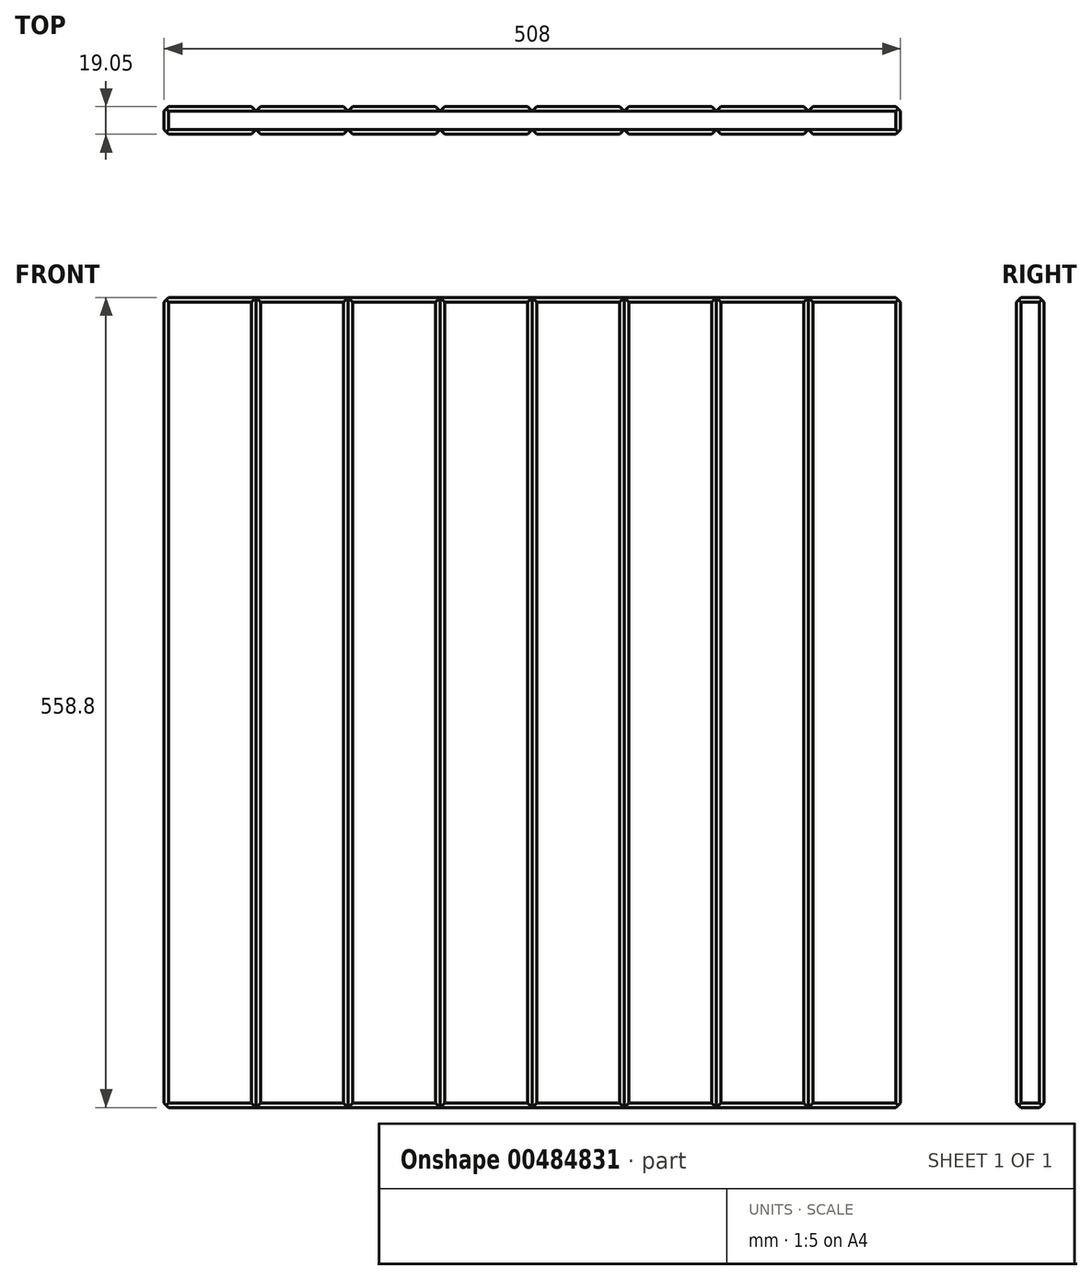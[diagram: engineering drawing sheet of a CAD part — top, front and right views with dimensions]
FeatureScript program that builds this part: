
annotation { "Feature Type Name" : "Feature", "Feature Type Description" : "" }
export const myFeature = defineFeature(function(context is Context, id is Id, definition is map)
    precondition{}
    {
        {
            var Q0;
            Q0=qCreatedBy(makeId("Front.planeOp"),FACE);
            var sketch = newSketch(context, id + "F0", { "sketchPlane" : qUnion([Q0])});
            skLineSegment(sketch, "E0.bottom", {"start": v(254, 279.4) * mm, "end": v(-254, 279.4) * mm});
            skLineSegment(sketch, "E0.top", {"start": v(254, -279.4) * mm, "end": v(-254, -279.4) * mm});
            skLineSegment(sketch, "E0.left", {"start": v(254, 279.4) * mm, "end": v(254, -279.4) * mm});
            skLineSegment(sketch, "E0.right", {"start": v(-254, 279.4) * mm, "end": v(-254, -279.4) * mm});
            skPoint(sketch, "E0.middle", {"position": v(0, 0) * mm});
            skSolve(sketch);
        }
        {
            var Q0;
            Q0 = qSketchRegion(id + "F0", true);
            extrude(context, id + "F1", {"entities" : qUnion([Q0]), "depth" : 19.05 * mm});
        }
        {
            var Q0;
            Q0=makeQuery(id+"F1.opExtrude","SWEPT_FACE",FACE,{"disambiguationData":[OSD([sQuery(id+"F0.wireOp",EDGE,"E0.top")])]});
            var sketch = newSketch(context, id + "F2", { "sketchPlane" : qUnion([Q0])});
            skLineSegment(sketch, "E1", {"start": v(-254, 19.05) * mm, "end": v(-190.5, 19.05) * mm});
            skLineSegment(sketch, "E2", {"start": v(-190.5, 19.05) * mm, "end": v(-127, 19.05) * mm});
            skLineSegment(sketch, "E3", {"start": v(-127, 19.05) * mm, "end": v(-63.5, 19.05) * mm});
            skLineSegment(sketch, "E4", {"start": v(-63.5, 19.05) * mm, "end": v(0, 19.05) * mm});
            skLineSegment(sketch, "E5", {"start": v(0, 19.05) * mm, "end": v(63.5, 19.05) * mm});
            skLineSegment(sketch, "E6", {"start": v(63.5, 19.05) * mm, "end": v(127, 19.05) * mm});
            skLineSegment(sketch, "E7", {"start": v(127, 19.05) * mm, "end": v(190.5, 19.05) * mm});
            skLineSegment(sketch, "E8", {"start": v(-254, 19.05) * mm, "end": v(-254, 15.88) * mm});
            skLineSegment(sketch, "E9", {"start": v(190.5, 19.05) * mm, "end": v(187.32, 19.05) * mm});
            skLineSegment(sketch, "E10", {"start": v(187.32, 19.05) * mm, "end": v(193.67, 19.05) * mm});
            skLineSegment(sketch, "E11", {"start": v(193.67, 19.05) * mm, "end": v(190.5, 15.88) * mm});
            skLineSegment(sketch, "E12", {"start": v(190.5, 15.88) * mm, "end": v(187.32, 19.05) * mm});
            skLineSegment(sketch, "E13.1.0.0", {"start": v(127, 15.88) * mm, "end": v(123.83, 19.05) * mm});
            skLineSegment(sketch, "E13.1.0.1", {"start": v(130.17, 19.05) * mm, "end": v(127, 15.88) * mm});
            skLineSegment(sketch, "E13.1.0.2", {"start": v(123.82, 19.05) * mm, "end": v(130.17, 19.05) * mm});
            skLineSegment(sketch, "E13.1.0.3", {"start": v(127, 19.05) * mm, "end": v(123.82, 19.05) * mm});
            skLineSegment(sketch, "E13.2.0.0", {"start": v(63.5, 15.87) * mm, "end": v(60.33, 19.05) * mm});
            skLineSegment(sketch, "E13.2.0.1", {"start": v(66.67, 19.05) * mm, "end": v(63.5, 15.88) * mm});
            skLineSegment(sketch, "E13.2.0.2", {"start": v(60.32, 19.05) * mm, "end": v(66.67, 19.05) * mm});
            skLineSegment(sketch, "E13.2.0.3", {"start": v(63.5, 19.05) * mm, "end": v(60.32, 19.05) * mm});
            skLineSegment(sketch, "E13.3.0.0", {"start": v(0, 15.87) * mm, "end": v(-3.17, 19.05) * mm});
            skLineSegment(sketch, "E13.3.0.1", {"start": v(3.17, 19.05) * mm, "end": v(0, 15.88) * mm});
            skLineSegment(sketch, "E13.3.0.2", {"start": v(-3.18, 19.05) * mm, "end": v(3.17, 19.05) * mm});
            skLineSegment(sketch, "E13.3.0.3", {"start": v(0, 19.05) * mm, "end": v(-3.18, 19.05) * mm});
            skLineSegment(sketch, "E13.4.0.0", {"start": v(-63.5, 15.87) * mm, "end": v(-66.68, 19.05) * mm});
            skLineSegment(sketch, "E13.4.0.1", {"start": v(-60.33, 19.05) * mm, "end": v(-63.5, 15.88) * mm});
            skLineSegment(sketch, "E13.4.0.2", {"start": v(-66.68, 19.05) * mm, "end": v(-60.33, 19.05) * mm});
            skLineSegment(sketch, "E13.4.0.3", {"start": v(-63.5, 19.05) * mm, "end": v(-66.68, 19.05) * mm});
            skLineSegment(sketch, "E13.5.0.0", {"start": v(-127, 15.87) * mm, "end": v(-130.18, 19.05) * mm});
            skLineSegment(sketch, "E13.5.0.1", {"start": v(-123.83, 19.05) * mm, "end": v(-127, 15.88) * mm});
            skLineSegment(sketch, "E13.5.0.2", {"start": v(-130.18, 19.05) * mm, "end": v(-123.83, 19.05) * mm});
            skLineSegment(sketch, "E13.5.0.3", {"start": v(-127, 19.05) * mm, "end": v(-130.18, 19.05) * mm});
            skLineSegment(sketch, "E13.6.0.0", {"start": v(-190.5, 15.87) * mm, "end": v(-193.68, 19.05) * mm});
            skLineSegment(sketch, "E13.6.0.1", {"start": v(-187.33, 19.05) * mm, "end": v(-190.5, 15.87) * mm});
            skLineSegment(sketch, "E13.6.0.2", {"start": v(-193.68, 19.05) * mm, "end": v(-187.33, 19.05) * mm});
            skLineSegment(sketch, "E13.6.0.3", {"start": v(-190.5, 19.05) * mm, "end": v(-193.68, 19.05) * mm});
            skSolve(sketch);
        }
        {
            var Q0;
            Q0 = qSketchRegion(id + "F2", true);
            extrude(context, id + "F3", {"entities" : qUnion([Q0]), "operationType" : NewBodyOperationType.REMOVE, "endBound" : BoundingType.THROUGH_ALL, "oppositeDirection" : true, "depth" : 25.4 * mm});
        }
        {
            var Q0;
            Q0=makeQuery(id+"F1.opExtrude","CAP_EDGE",EDGE,{"disambiguationData":[OSD([sQuery(id+"F0.wireOp",EDGE,"E0.right")])],"isStart":false});
            var Q1;
            {var subQ0=sQuery(id+"F0.wireOp",EDGE,"E0.right");var subQ1=sQuery(id+"F0.wireOp",EDGE,"E0.top");Q1=makeQuery(id+"F3.boolean.opBoolean","SPLIT",EDGE,{"disambiguationData":[TD([makeQuery(id+"F1.opExtrude","SWEPT_FACE",FACE,{"disambiguationData":[OSD([subQ0])]})])],"derivedFrom":makeQuery(id+"F1.opExtrude","CAP_EDGE",EDGE,{"disambiguationData":[OSD([subQ1])],"isStart":false})});}
            var Q2;
            {var subQ0=sQuery(id+"F0.wireOp",EDGE,"E0.top");Q2=makeQuery(id+"F3.boolean.opBoolean","SPLIT",EDGE,{"disambiguationData":[TD([makeQuery(id+"F3.opExtrude","SWEPT_FACE",FACE,{"disambiguationData":[OSD([sQuery(id+"F2.wireOp",EDGE,"E13.5.0.0")])]})])],"derivedFrom":makeQuery(id+"F1.opExtrude","CAP_EDGE",EDGE,{"disambiguationData":[OSD([subQ0])],"isStart":false})});}
            var Q3;
            {var subQ0=sQuery(id+"F0.wireOp",EDGE,"E0.top");Q3=makeQuery(id+"F3.boolean.opBoolean","SPLIT",EDGE,{"disambiguationData":[TD([makeQuery(id+"F3.opExtrude","SWEPT_FACE",FACE,{"disambiguationData":[OSD([sQuery(id+"F2.wireOp",EDGE,"E13.4.0.0")])]})])],"derivedFrom":makeQuery(id+"F1.opExtrude","CAP_EDGE",EDGE,{"disambiguationData":[OSD([subQ0])],"isStart":false})});}
            var Q4;
            {var subQ0=sQuery(id+"F0.wireOp",EDGE,"E0.top");Q4=makeQuery(id+"F3.boolean.opBoolean","SPLIT",EDGE,{"disambiguationData":[TD([makeQuery(id+"F3.opExtrude","SWEPT_FACE",FACE,{"disambiguationData":[OSD([sQuery(id+"F2.wireOp",EDGE,"E13.3.0.0")])]})])],"derivedFrom":makeQuery(id+"F1.opExtrude","CAP_EDGE",EDGE,{"disambiguationData":[OSD([subQ0])],"isStart":false})});}
            var Q5;
            {var subQ0=sQuery(id+"F0.wireOp",EDGE,"E0.top");Q5=makeQuery(id+"F3.boolean.opBoolean","SPLIT",EDGE,{"disambiguationData":[TD([makeQuery(id+"F3.opExtrude","SWEPT_FACE",FACE,{"disambiguationData":[OSD([sQuery(id+"F2.wireOp",EDGE,"E13.2.0.0")])]})])],"derivedFrom":makeQuery(id+"F1.opExtrude","CAP_EDGE",EDGE,{"disambiguationData":[OSD([subQ0])],"isStart":false})});}
            var Q6;
            {var subQ0=sQuery(id+"F0.wireOp",EDGE,"E0.top");Q6=makeQuery(id+"F3.boolean.opBoolean","SPLIT",EDGE,{"disambiguationData":[TD([makeQuery(id+"F3.opExtrude","SWEPT_FACE",FACE,{"disambiguationData":[OSD([sQuery(id+"F2.wireOp",EDGE,"E13.1.0.0")])]})])],"derivedFrom":makeQuery(id+"F1.opExtrude","CAP_EDGE",EDGE,{"disambiguationData":[OSD([subQ0])],"isStart":false})});}
            var Q7;
            {var subQ0=sQuery(id+"F0.wireOp",EDGE,"E0.top");Q7=makeQuery(id+"F3.boolean.opBoolean","SPLIT",EDGE,{"disambiguationData":[TD([makeQuery(id+"F3.opExtrude","SWEPT_FACE",FACE,{"disambiguationData":[OSD([sQuery(id+"F2.wireOp",EDGE,"E12")])]})])],"derivedFrom":makeQuery(id+"F1.opExtrude","CAP_EDGE",EDGE,{"disambiguationData":[OSD([subQ0])],"isStart":false})});}
            var Q8;
            {var subQ0=sQuery(id+"F0.wireOp",EDGE,"E0.left");var subQ1=sQuery(id+"F0.wireOp",EDGE,"E0.top");Q8=makeQuery(id+"F3.boolean.opBoolean","SPLIT",EDGE,{"disambiguationData":[TD([makeQuery(id+"F1.opExtrude","SWEPT_FACE",FACE,{"disambiguationData":[OSD([subQ0])]})])],"derivedFrom":makeQuery(id+"F1.opExtrude","CAP_EDGE",EDGE,{"disambiguationData":[OSD([subQ1])],"isStart":false})});}
            var Q9;
            Q9=makeQuery(id+"F1.opExtrude","CAP_EDGE",EDGE,{"disambiguationData":[OSD([sQuery(id+"F0.wireOp",EDGE,"E0.left")])],"isStart":false});
            var Q10;
            {var subQ0=sQuery(id+"F0.wireOp",EDGE,"E0.bottom");var subQ1=sQuery(id+"F0.wireOp",EDGE,"E0.left");Q10=makeQuery(id+"F3.boolean.opBoolean","SPLIT",EDGE,{"disambiguationData":[TD([makeQuery(id+"F1.opExtrude","SWEPT_FACE",FACE,{"disambiguationData":[OSD([subQ1])]})])],"derivedFrom":makeQuery(id+"F1.opExtrude","CAP_EDGE",EDGE,{"disambiguationData":[OSD([subQ0])],"isStart":false})});}
            var Q11;
            {var subQ0=sQuery(id+"F0.wireOp",EDGE,"E0.bottom");Q11=makeQuery(id+"F3.boolean.opBoolean","SPLIT",EDGE,{"disambiguationData":[TD([makeQuery(id+"F3.opExtrude","SWEPT_FACE",FACE,{"disambiguationData":[OSD([sQuery(id+"F2.wireOp",EDGE,"E12")])]})])],"derivedFrom":makeQuery(id+"F1.opExtrude","CAP_EDGE",EDGE,{"disambiguationData":[OSD([subQ0])],"isStart":false})});}
            var Q12;
            {var subQ0=sQuery(id+"F0.wireOp",EDGE,"E0.bottom");Q12=makeQuery(id+"F3.boolean.opBoolean","SPLIT",EDGE,{"disambiguationData":[TD([makeQuery(id+"F3.opExtrude","SWEPT_FACE",FACE,{"disambiguationData":[OSD([sQuery(id+"F2.wireOp",EDGE,"E13.1.0.0")])]})])],"derivedFrom":makeQuery(id+"F1.opExtrude","CAP_EDGE",EDGE,{"disambiguationData":[OSD([subQ0])],"isStart":false})});}
            var Q13;
            {var subQ0=sQuery(id+"F0.wireOp",EDGE,"E0.bottom");Q13=makeQuery(id+"F3.boolean.opBoolean","SPLIT",EDGE,{"disambiguationData":[TD([makeQuery(id+"F3.opExtrude","SWEPT_FACE",FACE,{"disambiguationData":[OSD([sQuery(id+"F2.wireOp",EDGE,"E13.2.0.0")])]})])],"derivedFrom":makeQuery(id+"F1.opExtrude","CAP_EDGE",EDGE,{"disambiguationData":[OSD([subQ0])],"isStart":false})});}
            var Q14;
            {var subQ0=sQuery(id+"F0.wireOp",EDGE,"E0.bottom");Q14=makeQuery(id+"F3.boolean.opBoolean","SPLIT",EDGE,{"disambiguationData":[TD([makeQuery(id+"F3.opExtrude","SWEPT_FACE",FACE,{"disambiguationData":[OSD([sQuery(id+"F2.wireOp",EDGE,"E13.3.0.0")])]})])],"derivedFrom":makeQuery(id+"F1.opExtrude","CAP_EDGE",EDGE,{"disambiguationData":[OSD([subQ0])],"isStart":false})});}
            var Q15;
            {var subQ0=sQuery(id+"F0.wireOp",EDGE,"E0.bottom");Q15=makeQuery(id+"F3.boolean.opBoolean","SPLIT",EDGE,{"disambiguationData":[TD([makeQuery(id+"F3.opExtrude","SWEPT_FACE",FACE,{"disambiguationData":[OSD([sQuery(id+"F2.wireOp",EDGE,"E13.4.0.0")])]})])],"derivedFrom":makeQuery(id+"F1.opExtrude","CAP_EDGE",EDGE,{"disambiguationData":[OSD([subQ0])],"isStart":false})});}
            var Q16;
            {var subQ0=sQuery(id+"F0.wireOp",EDGE,"E0.bottom");Q16=makeQuery(id+"F3.boolean.opBoolean","SPLIT",EDGE,{"disambiguationData":[TD([makeQuery(id+"F3.opExtrude","SWEPT_FACE",FACE,{"disambiguationData":[OSD([sQuery(id+"F2.wireOp",EDGE,"E13.5.0.0")])]})])],"derivedFrom":makeQuery(id+"F1.opExtrude","CAP_EDGE",EDGE,{"disambiguationData":[OSD([subQ0])],"isStart":false})});}
            var Q17;
            {var subQ0=sQuery(id+"F0.wireOp",EDGE,"E0.bottom");var subQ1=sQuery(id+"F0.wireOp",EDGE,"E0.right");Q17=makeQuery(id+"F3.boolean.opBoolean","SPLIT",EDGE,{"disambiguationData":[TD([makeQuery(id+"F1.opExtrude","SWEPT_FACE",FACE,{"disambiguationData":[OSD([subQ1])]})])],"derivedFrom":makeQuery(id+"F1.opExtrude","CAP_EDGE",EDGE,{"disambiguationData":[OSD([subQ0])],"isStart":false})});}
            chamfer(context, id + "F4", {"entities" : qUnion([Q0, Q1, Q2, Q3, Q4, Q5, Q6, Q7, Q8, Q9, Q10, Q11, Q12, Q13, Q14, Q15, Q16, Q17]), "width" : 3.17 * mm, "tangentPropagation" : true});
        }
        {
            var Q0;
            Q0=makeQuery(id+"F1.opExtrude","SWEPT_EDGE",EDGE,{"disambiguationData":[OSD([sQuery(id+"F0.wireOp",EDGE,"E0.bottom"),sQuery(id+"F0.wireOp",EDGE,"E0.right")])]});
            var Q1;
            Q1=makeQuery(id+"F1.opExtrude","SWEPT_EDGE",EDGE,{"disambiguationData":[OSD([sQuery(id+"F0.wireOp",EDGE,"E0.top"),sQuery(id+"F0.wireOp",EDGE,"E0.right")])]});
            var Q2;
            Q2=makeQuery(id+"F1.opExtrude","SWEPT_EDGE",EDGE,{"disambiguationData":[OSD([sQuery(id+"F0.wireOp",EDGE,"E0.top"),sQuery(id+"F0.wireOp",EDGE,"E0.left")])]});
            var Q3;
            Q3=makeQuery(id+"F1.opExtrude","SWEPT_EDGE",EDGE,{"disambiguationData":[OSD([sQuery(id+"F0.wireOp",EDGE,"E0.bottom"),sQuery(id+"F0.wireOp",EDGE,"E0.left")])]});
            chamfer(context, id + "F5", {"entities" : qUnion([Q0, Q1, Q2, Q3]), "width" : 3.17 * mm, "tangentPropagation" : true});
        }
        {
            var Q0;
            Q0=makeQuery(id+"F1.opExtrude","SWEPT_FACE",FACE,{"disambiguationData":[OSD([sQuery(id+"F0.wireOp",EDGE,"E0.top")])]});
            var sketch = newSketch(context, id + "F6", { "sketchPlane" : qUnion([Q0])});
            skLineSegment(sketch, "E14", {"start": v(-190.5, 0) * mm, "end": v(-193.68, 0) * mm});
            skLineSegment(sketch, "E15", {"start": v(-193.68, 0) * mm, "end": v(-187.33, 0) * mm});
            skLineSegment(sketch, "E16", {"start": v(-190.5, 3.17) * mm, "end": v(-193.68, 0) * mm});
            skLineSegment(sketch, "E17", {"start": v(-190.5, 3.17) * mm, "end": v(-187.33, 0) * mm});
            skLineSegment(sketch, "E18.1.0.0", {"start": v(-127, 3.17) * mm, "end": v(-130.18, 0) * mm});
            skLineSegment(sketch, "E18.1.0.1", {"start": v(-127, 3.17) * mm, "end": v(-123.83, 0) * mm});
            skLineSegment(sketch, "E18.1.0.2", {"start": v(-130.18, 0) * mm, "end": v(-123.83, 0) * mm});
            skLineSegment(sketch, "E18.1.0.3", {"start": v(-127, 0) * mm, "end": v(-130.18, 0) * mm});
            skLineSegment(sketch, "E18.2.0.0", {"start": v(-63.5, 3.17) * mm, "end": v(-66.68, 0) * mm});
            skLineSegment(sketch, "E18.2.0.1", {"start": v(-63.5, 3.17) * mm, "end": v(-60.33, 0) * mm});
            skLineSegment(sketch, "E18.2.0.2", {"start": v(-66.68, 0) * mm, "end": v(-60.33, 0) * mm});
            skLineSegment(sketch, "E18.2.0.3", {"start": v(-63.5, 0) * mm, "end": v(-66.68, 0) * mm});
            skLineSegment(sketch, "E18.3.0.0", {"start": v(0, 3.17) * mm, "end": v(-3.18, 0) * mm});
            skLineSegment(sketch, "E18.3.0.1", {"start": v(0, 3.17) * mm, "end": v(3.17, 0) * mm});
            skLineSegment(sketch, "E18.3.0.2", {"start": v(-3.18, 0) * mm, "end": v(3.17, 0) * mm});
            skLineSegment(sketch, "E18.3.0.3", {"start": v(0, 0) * mm, "end": v(-3.18, 0) * mm});
            skLineSegment(sketch, "E18.4.0.0", {"start": v(63.5, 3.17) * mm, "end": v(60.32, 0) * mm});
            skLineSegment(sketch, "E18.4.0.1", {"start": v(63.5, 3.17) * mm, "end": v(66.67, 0) * mm});
            skLineSegment(sketch, "E18.4.0.2", {"start": v(60.32, 0) * mm, "end": v(66.67, 0) * mm});
            skLineSegment(sketch, "E18.4.0.3", {"start": v(63.5, 0) * mm, "end": v(60.32, 0) * mm});
            skLineSegment(sketch, "E18.5.0.0", {"start": v(127, 3.17) * mm, "end": v(123.82, 0) * mm});
            skLineSegment(sketch, "E18.5.0.1", {"start": v(127, 3.17) * mm, "end": v(130.17, 0) * mm});
            skLineSegment(sketch, "E18.5.0.2", {"start": v(123.82, 0) * mm, "end": v(130.17, 0) * mm});
            skLineSegment(sketch, "E18.5.0.3", {"start": v(127, 0) * mm, "end": v(123.82, 0) * mm});
            skLineSegment(sketch, "E18.6.0.0", {"start": v(190.5, 3.17) * mm, "end": v(187.32, 0) * mm});
            skLineSegment(sketch, "E18.6.0.1", {"start": v(190.5, 3.17) * mm, "end": v(193.67, 0) * mm});
            skLineSegment(sketch, "E18.6.0.2", {"start": v(187.32, 0) * mm, "end": v(193.67, 0) * mm});
            skLineSegment(sketch, "E18.6.0.3", {"start": v(190.5, 0) * mm, "end": v(187.32, 0) * mm});
            skSolve(sketch);
        }
        {
            var Q0;
            Q0 = qSketchRegion(id + "F6", true);
            extrude(context, id + "F7", {"entities" : qUnion([Q0]), "operationType" : NewBodyOperationType.REMOVE, "endBound" : BoundingType.THROUGH_ALL, "oppositeDirection" : true, "depth" : 25.4 * mm});
        }
        {
            var Q0;
            {var subQ1=sQuery(id+"F0.wireOp",EDGE,"E0.top");Q0=makeQuery(id+"F7.boolean.opBoolean","SPLIT",EDGE,{"disambiguationData":[TD([makeQuery(id+"F7.opExtrude","SWEPT_FACE",FACE,{"disambiguationData":[OSD([sQuery(id+"F6.wireOp",EDGE,"E16")])]})])],"derivedFrom":makeQuery(id+"F1.opExtrude","CAP_EDGE",EDGE,{"disambiguationData":[OSD([subQ1])],"isStart":true})});}
            var Q1;
            Q1=makeQuery(id+"F1.opExtrude","CAP_EDGE",EDGE,{"disambiguationData":[OSD([sQuery(id+"F0.wireOp",EDGE,"E0.right")])],"isStart":true});
            var Q2;
            {var subQ0=sQuery(id+"F0.wireOp",EDGE,"E0.top");Q2=makeQuery(id+"F7.boolean.opBoolean","SPLIT",EDGE,{"disambiguationData":[TD([makeQuery(id+"F7.opExtrude","SWEPT_FACE",FACE,{"disambiguationData":[OSD([sQuery(id+"F6.wireOp",EDGE,"E17")])]})])],"derivedFrom":makeQuery(id+"F1.opExtrude","CAP_EDGE",EDGE,{"disambiguationData":[OSD([subQ0])],"isStart":true})});}
            var Q3;
            {var subQ0=sQuery(id+"F0.wireOp",EDGE,"E0.top");Q3=makeQuery(id+"F7.boolean.opBoolean","SPLIT",EDGE,{"disambiguationData":[TD([makeQuery(id+"F7.opExtrude","SWEPT_FACE",FACE,{"disambiguationData":[OSD([sQuery(id+"F6.wireOp",EDGE,"E18.1.0.1")])]})])],"derivedFrom":makeQuery(id+"F1.opExtrude","CAP_EDGE",EDGE,{"disambiguationData":[OSD([subQ0])],"isStart":true})});}
            var Q4;
            {var subQ0=sQuery(id+"F0.wireOp",EDGE,"E0.top");Q4=makeQuery(id+"F7.boolean.opBoolean","SPLIT",EDGE,{"disambiguationData":[TD([makeQuery(id+"F7.opExtrude","SWEPT_FACE",FACE,{"disambiguationData":[OSD([sQuery(id+"F6.wireOp",EDGE,"E18.2.0.1")])]})])],"derivedFrom":makeQuery(id+"F1.opExtrude","CAP_EDGE",EDGE,{"disambiguationData":[OSD([subQ0])],"isStart":true})});}
            var Q5;
            {var subQ0=sQuery(id+"F0.wireOp",EDGE,"E0.top");Q5=makeQuery(id+"F7.boolean.opBoolean","SPLIT",EDGE,{"disambiguationData":[TD([makeQuery(id+"F7.opExtrude","SWEPT_FACE",FACE,{"disambiguationData":[OSD([sQuery(id+"F6.wireOp",EDGE,"E18.3.0.1")])]})])],"derivedFrom":makeQuery(id+"F1.opExtrude","CAP_EDGE",EDGE,{"disambiguationData":[OSD([subQ0])],"isStart":true})});}
            var Q6;
            {var subQ0=sQuery(id+"F0.wireOp",EDGE,"E0.top");Q6=makeQuery(id+"F7.boolean.opBoolean","SPLIT",EDGE,{"disambiguationData":[TD([makeQuery(id+"F7.opExtrude","SWEPT_FACE",FACE,{"disambiguationData":[OSD([sQuery(id+"F6.wireOp",EDGE,"E18.4.0.1")])]})])],"derivedFrom":makeQuery(id+"F1.opExtrude","CAP_EDGE",EDGE,{"disambiguationData":[OSD([subQ0])],"isStart":true})});}
            var Q7;
            {var subQ0=sQuery(id+"F0.wireOp",EDGE,"E0.top");Q7=makeQuery(id+"F7.boolean.opBoolean","SPLIT",EDGE,{"disambiguationData":[TD([makeQuery(id+"F7.opExtrude","SWEPT_FACE",FACE,{"disambiguationData":[OSD([sQuery(id+"F6.wireOp",EDGE,"E18.5.0.1")])]})])],"derivedFrom":makeQuery(id+"F1.opExtrude","CAP_EDGE",EDGE,{"disambiguationData":[OSD([subQ0])],"isStart":true})});}
            var Q8;
            {var subQ1=sQuery(id+"F0.wireOp",EDGE,"E0.top");Q8=makeQuery(id+"F7.boolean.opBoolean","SPLIT",EDGE,{"disambiguationData":[TD([makeQuery(id+"F7.opExtrude","SWEPT_FACE",FACE,{"disambiguationData":[OSD([sQuery(id+"F6.wireOp",EDGE,"E18.6.0.1")])]})])],"derivedFrom":makeQuery(id+"F1.opExtrude","CAP_EDGE",EDGE,{"disambiguationData":[OSD([subQ1])],"isStart":true})});}
            var Q9;
            Q9=makeQuery(id+"F1.opExtrude","CAP_EDGE",EDGE,{"disambiguationData":[OSD([sQuery(id+"F0.wireOp",EDGE,"E0.left")])],"isStart":true});
            var Q10;
            {var subQ0=sQuery(id+"F0.wireOp",EDGE,"E0.bottom");Q10=makeQuery(id+"F7.boolean.opBoolean","SPLIT",EDGE,{"disambiguationData":[TD([makeQuery(id+"F7.opExtrude","SWEPT_FACE",FACE,{"disambiguationData":[OSD([sQuery(id+"F6.wireOp",EDGE,"E18.6.0.1")])]})])],"derivedFrom":makeQuery(id+"F1.opExtrude","CAP_EDGE",EDGE,{"disambiguationData":[OSD([subQ0])],"isStart":true})});}
            var Q11;
            {var subQ0=sQuery(id+"F0.wireOp",EDGE,"E0.bottom");Q11=makeQuery(id+"F7.boolean.opBoolean","SPLIT",EDGE,{"disambiguationData":[TD([makeQuery(id+"F7.opExtrude","SWEPT_FACE",FACE,{"disambiguationData":[OSD([sQuery(id+"F6.wireOp",EDGE,"E18.5.0.1")])]})])],"derivedFrom":makeQuery(id+"F1.opExtrude","CAP_EDGE",EDGE,{"disambiguationData":[OSD([subQ0])],"isStart":true})});}
            var Q12;
            {var subQ0=sQuery(id+"F0.wireOp",EDGE,"E0.bottom");Q12=makeQuery(id+"F7.boolean.opBoolean","SPLIT",EDGE,{"disambiguationData":[TD([makeQuery(id+"F7.opExtrude","SWEPT_FACE",FACE,{"disambiguationData":[OSD([sQuery(id+"F6.wireOp",EDGE,"E18.4.0.1")])]})])],"derivedFrom":makeQuery(id+"F1.opExtrude","CAP_EDGE",EDGE,{"disambiguationData":[OSD([subQ0])],"isStart":true})});}
            var Q13;
            {var subQ0=sQuery(id+"F0.wireOp",EDGE,"E0.bottom");Q13=makeQuery(id+"F7.boolean.opBoolean","SPLIT",EDGE,{"disambiguationData":[TD([makeQuery(id+"F7.opExtrude","SWEPT_FACE",FACE,{"disambiguationData":[OSD([sQuery(id+"F6.wireOp",EDGE,"E18.3.0.1")])]})])],"derivedFrom":makeQuery(id+"F1.opExtrude","CAP_EDGE",EDGE,{"disambiguationData":[OSD([subQ0])],"isStart":true})});}
            var Q14;
            {var subQ0=sQuery(id+"F0.wireOp",EDGE,"E0.bottom");Q14=makeQuery(id+"F7.boolean.opBoolean","SPLIT",EDGE,{"disambiguationData":[TD([makeQuery(id+"F7.opExtrude","SWEPT_FACE",FACE,{"disambiguationData":[OSD([sQuery(id+"F6.wireOp",EDGE,"E18.2.0.1")])]})])],"derivedFrom":makeQuery(id+"F1.opExtrude","CAP_EDGE",EDGE,{"disambiguationData":[OSD([subQ0])],"isStart":true})});}
            var Q15;
            {var subQ0=sQuery(id+"F0.wireOp",EDGE,"E0.bottom");Q15=makeQuery(id+"F7.boolean.opBoolean","SPLIT",EDGE,{"disambiguationData":[TD([makeQuery(id+"F7.opExtrude","SWEPT_FACE",FACE,{"disambiguationData":[OSD([sQuery(id+"F6.wireOp",EDGE,"E18.1.0.1")])]})])],"derivedFrom":makeQuery(id+"F1.opExtrude","CAP_EDGE",EDGE,{"disambiguationData":[OSD([subQ0])],"isStart":true})});}
            var Q16;
            {var subQ0=sQuery(id+"F0.wireOp",EDGE,"E0.bottom");Q16=makeQuery(id+"F7.boolean.opBoolean","SPLIT",EDGE,{"disambiguationData":[TD([makeQuery(id+"F7.opExtrude","SWEPT_FACE",FACE,{"disambiguationData":[OSD([sQuery(id+"F6.wireOp",EDGE,"E17")])]})])],"derivedFrom":makeQuery(id+"F1.opExtrude","CAP_EDGE",EDGE,{"disambiguationData":[OSD([subQ0])],"isStart":true})});}
            var Q17;
            {var subQ0=sQuery(id+"F0.wireOp",EDGE,"E0.bottom");Q17=makeQuery(id+"F7.boolean.opBoolean","SPLIT",EDGE,{"disambiguationData":[TD([makeQuery(id+"F7.opExtrude","SWEPT_FACE",FACE,{"disambiguationData":[OSD([sQuery(id+"F6.wireOp",EDGE,"E16")])]})])],"derivedFrom":makeQuery(id+"F1.opExtrude","CAP_EDGE",EDGE,{"disambiguationData":[OSD([subQ0])],"isStart":true})});}
            chamfer(context, id + "F8", {"entities" : qUnion([Q0, Q1, Q2, Q3, Q4, Q5, Q6, Q7, Q8, Q9, Q10, Q11, Q12, Q13, Q14, Q15, Q16, Q17]), "width" : 3.17 * mm, "tangentPropagation" : true});
        }
    });
